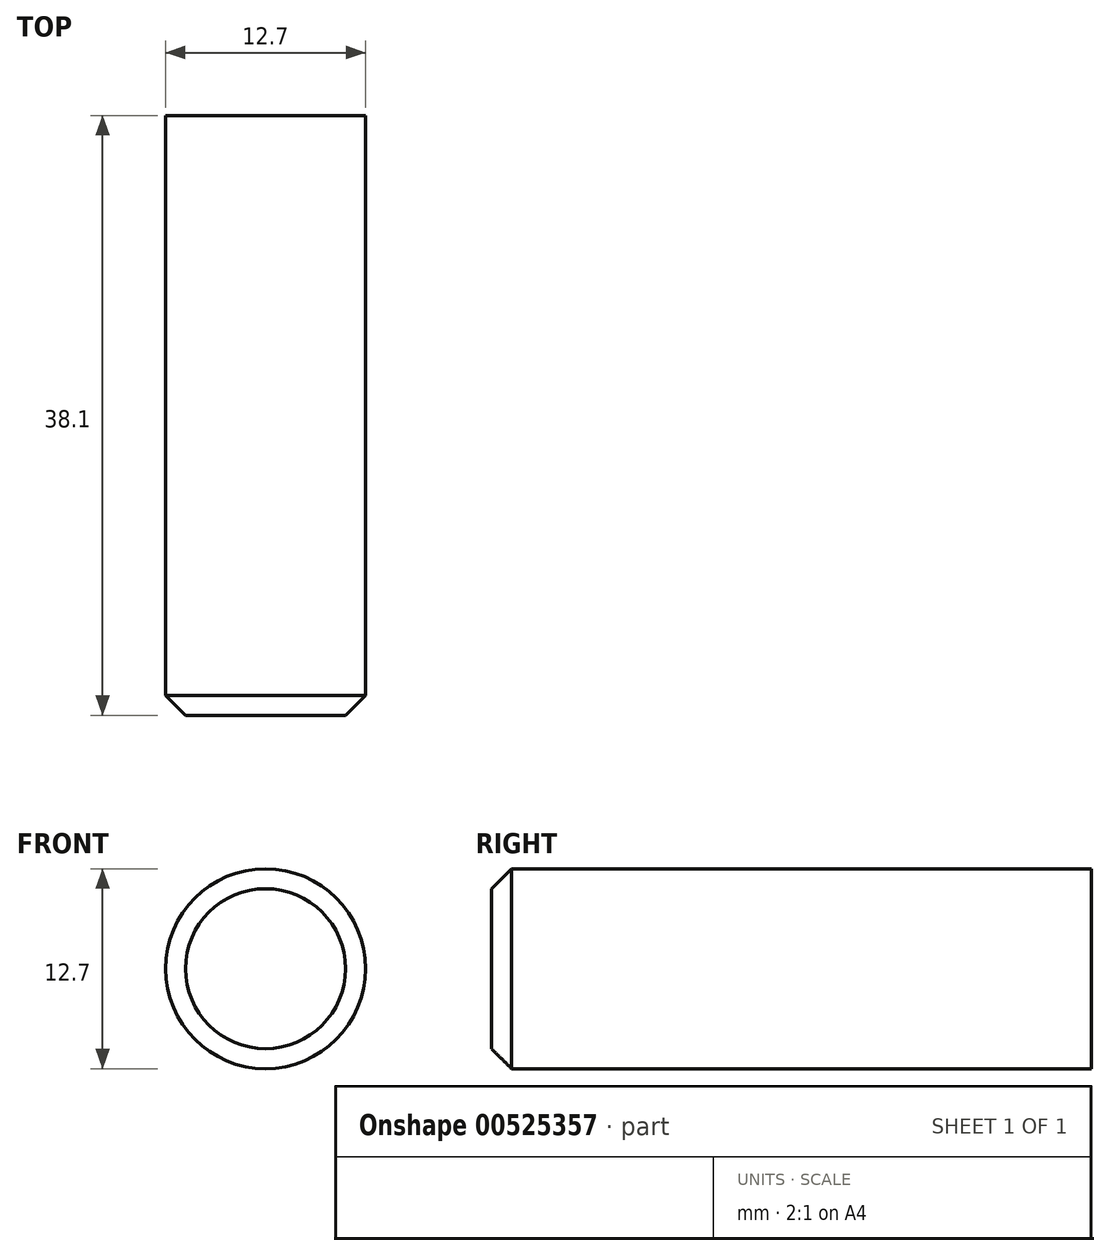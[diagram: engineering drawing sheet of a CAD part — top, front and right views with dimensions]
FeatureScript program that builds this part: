
annotation { "Feature Type Name" : "Feature", "Feature Type Description" : "" }
export const myFeature = defineFeature(function(context is Context, id is Id, definition is map)
    precondition{}
    {
        {
            var Q0;
            Q0=qCreatedBy(makeId("Front.planeOp"),FACE);
            var sketch = newSketch(context, id + "F0", { "sketchPlane" : qUnion([Q0])});
            skCircle(sketch, "E0", {"center": v(-1.04, 0) * mm, "radius": 6.35 * mm});
            skSolve(sketch);
        }
        {
            var Q0;
            Q0 = qSketchRegion(id + "F0", true);
            extrude(context, id + "F1", {"entities" : qUnion([Q0]), "depth" : 38.1 * mm, "offsetDistance" : 25.4 * mm});
        }
        {
            var Q0;
            Q0=makeQuery(id+"F1.opExtrude","CAP_EDGE",EDGE,{"disambiguationData":[OSD([sQuery(id+"F0.wireOp",EDGE,"E0")])],"isStart":false});
            chamfer(context, id + "F2", {"entities" : qUnion([Q0]), "width" : 1.27 * mm, "tangentPropagation" : true});
        }
    });
